# Revit family: Lavatory-Sink-Excel_Dryer-XLERATORsync_Double_Basin
name_source: partatom
category: Specialty Equipment
revit_build: Autodesk Revit 2018 (Build: 20190510_1515(x64)
units: mm (PartAtom-declared; Revit-internal decimal feet)

## family parameters
Cut with Voids When Loaded = No
Host = Face
OmniClass Number = 23.45.05.14.14
OmniClass Title = Sinks/Lavatories
Part Type = Normal
Room Calculation Point = No
Round Connector Dimension = Use Diameter
Shared = No

## types (2) — shared parameters
Apparent Load = 500 VA
Cabinet Finish = Metal - Excel Dryer - Zink Alloy - Textured Graphite
Cold Water Connection Diameter = 0' - 0 1/2"
Cost Information = http://www.exceldryer.com
Counter Finish = Quartz Surface - Excel Dryer - Jasmine White
Default Elevation = 0' - 0"
Depth = 2' - 0"
Description = XLERATORsync® - 2 Basin
Drain Connection Diameter = 0' - 1"
Fixture Finish = Metal - Excel Dryer - Chrome - Polished
Frequency = 60 Hz
Height = 2' - 10"
Hot Water Connection Diameter = 0' - 0 1/2"
Installation URL = https://www.exceldryer.com
Manufacturer = Excel Dryer
Manufacturer Fax Number = 1-413-525-2853
Number of Poles = 1
Panel Material = Metal - Excel Dryer - Zinc Alloy - White
Phase = 1
Power Factor = 1
Product Documentation Link = https://www.exceldryer.com
Product Name = XLERATORsync®
Product Page URL = https://www.exceldryer.com
Splash Guard Material = Quartz Surface - Excel Dryer - Jasmine White
URL = http://www.exceldryer.com
Version = 2018 - v1.0b
Voltage = 120 V
Warranty URL = https://www.exceldryer.com
Watts = 500 W

## per-type parameters (varying)
| type | Assembly Code | Full Trough Sink | Individual Cast Sink | Keynote | Model | Sink Material |
| Cast Sink | D2010 | No | Yes | 22 42 16 | Basin Sink | Solid Surface - DuPont - Corian - Glacier White 1/2" (12mm) |
| Trough Sink (Infinity Drain) |  | Yes | No |  | Channel Sink | Quartz Surface - Excel Dryer - Jasmine White |

## geometry (parser evidence)
native form markers: Sweep x12
no freeform markers — native parametric forms only
